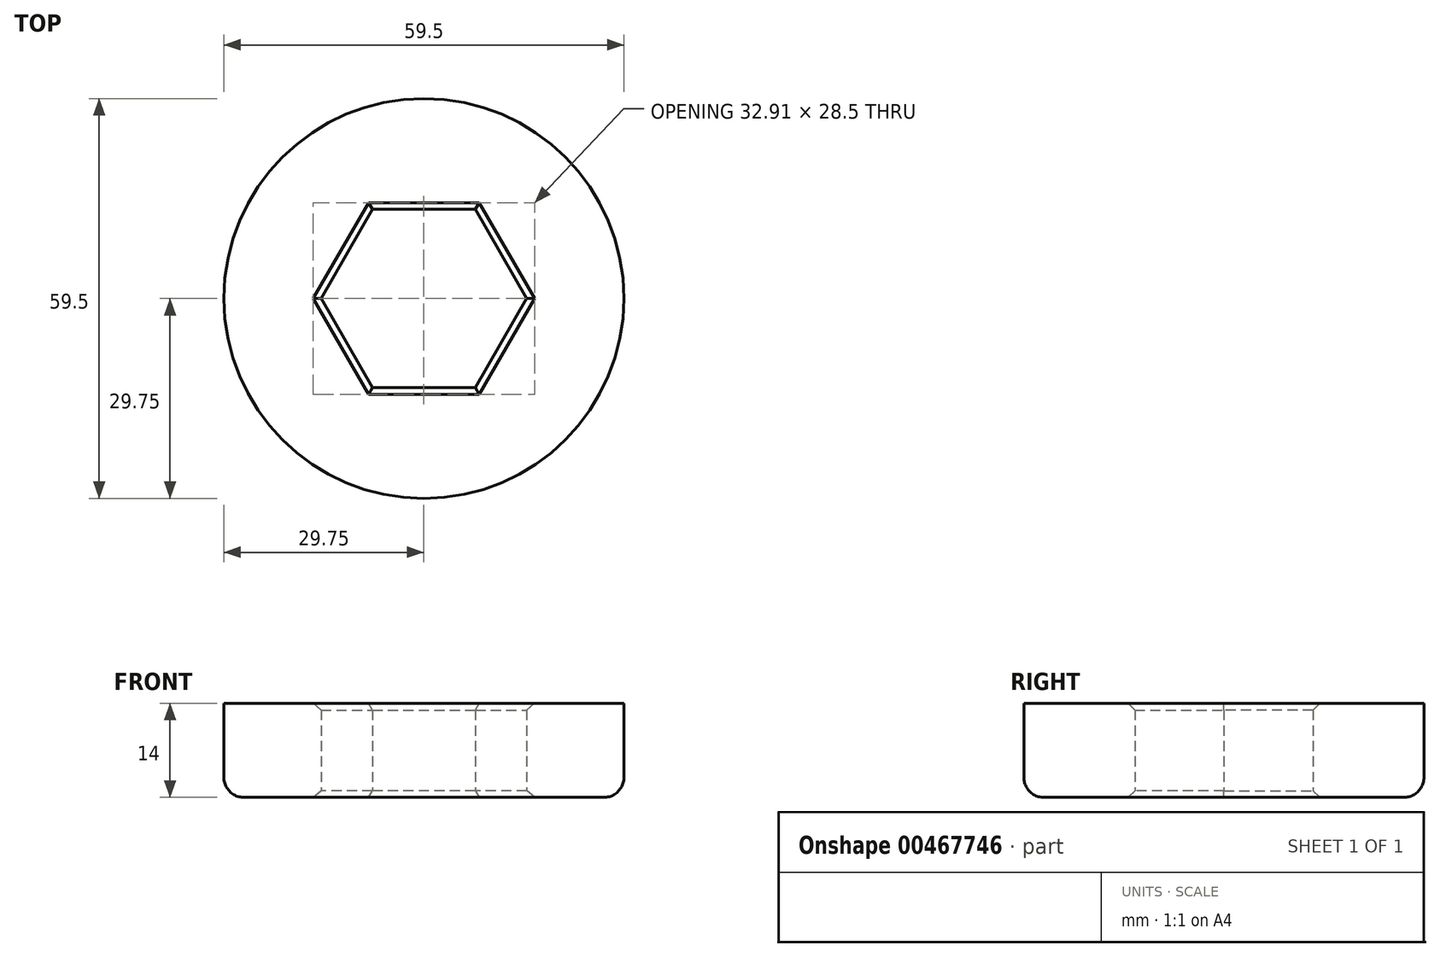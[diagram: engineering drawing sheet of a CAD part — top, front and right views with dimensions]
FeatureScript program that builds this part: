
annotation { "Feature Type Name" : "Feature", "Feature Type Description" : "" }
export const myFeature = defineFeature(function(context is Context, id is Id, definition is map)
    precondition{}
    {
        {
            var Q0;
            Q0=qCreatedBy(makeId("Top.planeOp"),FACE);
            var sketch = newSketch(context, id + "F0", { "sketchPlane" : qUnion([Q0])});
            skCircle(sketch, "E0", {"center": v(0, 0) * mm, "radius": 29.75 * mm});
            skCircle(sketch, "E1.cCircle", {"center": v(0, 0) * mm, "radius": 13.25 * mm, "construction": true});
            skLineSegment(sketch, "E1.0", {"start": v(7.65, -13.25) * mm, "end": v(-7.65, -13.25) * mm});
            skLineSegment(sketch, "E1.1", {"start": v(-7.65, -13.25) * mm, "end": v(-15.3, 0) * mm});
            skLineSegment(sketch, "E1.2", {"start": v(-15.3, 0) * mm, "end": v(-7.65, 13.25) * mm});
            skLineSegment(sketch, "E1.3", {"start": v(-7.65, 13.25) * mm, "end": v(7.65, 13.25) * mm});
            skLineSegment(sketch, "E1.4", {"start": v(7.65, 13.25) * mm, "end": v(15.3, 0) * mm});
            skLineSegment(sketch, "E1.5", {"start": v(15.3, 0) * mm, "end": v(7.65, -13.25) * mm});
            skPoint(sketch, "E1.0.midPoint", {"position": v(0, -13.25) * mm});
            skSolve(sketch);
        }
        {
            var Q0;
            Q0 = qSketchRegion(id + "F0", true);
            extrude(context, id + "F1", {"entities" : qUnion([Q0]), "depth" : 14 * mm});
        }
        {
            var Q0;
            Q0=makeQuery(id+"F1.opExtrude","CAP_EDGE",EDGE,{"disambiguationData":[OSD([sQuery(id+"F0.wireOp",EDGE,"E0")])],"isStart":true});
            fillet(context, id + "F2", {"entities" : qUnion([Q0]), "radius" : 3 * mm, "tangentPropagation" : true, "allowEdgeOverflow" : false});
        }
        {
            var Q0;
            Q0=makeQuery(id+"F1.opExtrude","CAP_EDGE",EDGE,{"disambiguationData":[OSD([sQuery(id+"F0.wireOp",EDGE,"E1.1")])],"isStart":false});
            var Q1;
            Q1=makeQuery(id+"F1.opExtrude","CAP_EDGE",EDGE,{"disambiguationData":[OSD([sQuery(id+"F0.wireOp",EDGE,"E1.2")])],"isStart":false});
            var Q2;
            Q2=makeQuery(id+"F1.opExtrude","CAP_EDGE",EDGE,{"disambiguationData":[OSD([sQuery(id+"F0.wireOp",EDGE,"E1.3")])],"isStart":false});
            var Q3;
            Q3=makeQuery(id+"F1.opExtrude","CAP_EDGE",EDGE,{"disambiguationData":[OSD([sQuery(id+"F0.wireOp",EDGE,"E1.5")])],"isStart":false});
            var Q4;
            Q4=makeQuery(id+"F1.opExtrude","CAP_EDGE",EDGE,{"disambiguationData":[OSD([sQuery(id+"F0.wireOp",EDGE,"E1.4")])],"isStart":true});
            var Q5;
            Q5=makeQuery(id+"F1.opExtrude","CAP_EDGE",EDGE,{"disambiguationData":[OSD([sQuery(id+"F0.wireOp",EDGE,"E1.0")])],"isStart":false});
            var Q6;
            Q6=makeQuery(id+"F1.opExtrude","CAP_EDGE",EDGE,{"disambiguationData":[OSD([sQuery(id+"F0.wireOp",EDGE,"E1.4")])],"isStart":false});
            chamfer(context, id + "F3", {"entities" : qUnion([Q0, Q1, Q2, Q3, Q4, Q5, Q6]), "width" : 1 * mm, "tangentPropagation" : true});
        }
        {
            var Q0;
            Q0=makeQuery(id+"F1.opExtrude","CAP_EDGE",EDGE,{"disambiguationData":[OSD([sQuery(id+"F0.wireOp",EDGE,"E1.5")])],"isStart":true});
            var Q1;
            Q1=makeQuery(id+"F1.opExtrude","CAP_EDGE",EDGE,{"disambiguationData":[OSD([sQuery(id+"F0.wireOp",EDGE,"E1.0")])],"isStart":true});
            var Q2;
            Q2=makeQuery(id+"F1.opExtrude","CAP_EDGE",EDGE,{"disambiguationData":[OSD([sQuery(id+"F0.wireOp",EDGE,"E1.1")])],"isStart":true});
            var Q3;
            Q3=makeQuery(id+"F1.opExtrude","CAP_EDGE",EDGE,{"disambiguationData":[OSD([sQuery(id+"F0.wireOp",EDGE,"E1.2")])],"isStart":true});
            var Q4;
            Q4=makeQuery(id+"F1.opExtrude","CAP_EDGE",EDGE,{"disambiguationData":[OSD([sQuery(id+"F0.wireOp",EDGE,"E1.3")])],"isStart":true});
            chamfer(context, id + "F4", {"entities" : qUnion([Q0, Q1, Q2, Q3, Q4]), "width" : 1 * mm, "tangentPropagation" : true});
        }
    });
